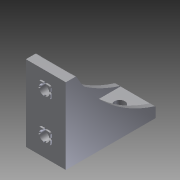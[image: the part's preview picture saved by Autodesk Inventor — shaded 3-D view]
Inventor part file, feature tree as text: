
AUTODESK INVENTOR PART (.ipt)
format: ipt  version: 2011 SP1 (Build 150282100, 282)  size: 227,840 bytes
history: native  units: mm
features: other x70, extrude x9, sketch x9, pattern_linear x2
ambient origin geometry x8: Origin, YZ Plane, XZ Plane, XY Plane, X Axis, Y Axis, Z Axis, Center Point
bodies: Solid1 (feature_tree)
feature tree (90):
  extrude  "Extrusion1"  Depth=15.0mm TaperAngle=0.0deg
  extrude  "Extrusion2"  Depth=5.0mm TaperAngle=0.0deg
  extrude  "Extrusion3"  Depth=5.0mm TaperAngle=0.0deg
  extrude  "Extrusion4"  Depth=0.8mm TaperAngle=0.0deg
  pattern_linear  "Rectangular Pattern1"  [2 undecoded]
  extrude  "Extrusion5"  [1 undecoded]
  pattern_linear  "Rectangular Pattern2"  [2 undecoded]
  extrude  "Extrusion6"  [1 undecoded]
  extrude  "Extrusion7"  [1 undecoded]
  extrude  "Extrusion8"  [1 undecoded]
  extrude  "Extrusion9"  [1 undecoded]
  other  "to_bolt_row_8_to_9_1_XY"
  other  "to_bolt_row_8_to_9_1_YZ"
  other  "to_bolt_row_8_to_9_1_ZX"
  other  "to_bolt_row_8_to_9_1_X"
  other  "to_bolt_row_8_to_9_1_Y"
  other  "to_bolt_row_8_to_9_1_Z"
  other  "to_bolt_row_8_to_9_1_Center"
  other  "to_bolt_row_8_to_9_2_XY"
  other  "to_bolt_row_8_to_9_2_YZ"
  other  "to_bolt_row_8_to_9_2_ZX"
  other  "to_bolt_row_8_to_9_2_X"
  other  "to_bolt_row_8_to_9_2_Y"
  other  "to_bolt_row_8_to_9_2_Z"
  other  "to_bolt_row_8_to_9_2_Center"
  other  "to_bolt_row_8_9_base_2_XY"
  other  "to_bolt_row_8_9_base_2_YZ"
  other  "to_bolt_row_8_9_base_2_ZX"
  other  "to_bolt_row_8_9_base_2_X"
  other  "to_bolt_row_8_9_base_2_Y"
  other  "to_bolt_row_8_9_base_2_Z"
  other  "to_bolt_row_8_9_base_2_Center"
  other  "to_bolt_row_8_9_base_1_XY"
  other  "to_bolt_row_8_9_base_1_YZ"
  other  "to_bolt_row_8_9_base_1_ZX"
  other  "to_bolt_row_8_9_base_1_X"
  other  "to_bolt_row_8_9_base_1_Y"
  other  "to_bolt_row_8_9_base_1_Z"
  other  "to_bolt_row_8_9_base_1_Center"
  other  "to_nut_row_8_to_9_2_XY"
  other  "to_nut_row_8_to_9_2_YZ"
  other  "to_nut_row_8_to_9_2_ZX"
  other  "to_nut_row_8_to_9_2_X"
  other  "to_nut_row_8_to_9_2_Y"
  other  "to_nut_row_8_to_9_2_Z"
  other  "to_nut_row_8_to_9_2_Center"
  other  "to_nut_row_8_to_9_1_XY"
  other  "to_nut_row_8_to_9_1_YZ"
  other  "to_nut_row_8_to_9_1_ZX"
  other  "to_nut_row_8_to_9_1_X"
  other  "to_nut_row_8_to_9_1_Y"
  other  "to_nut_row_8_to_9_1_Z"
  other  "to_nut_row_8_to_9_1_Center"
  other  "to_nut_row_8_9_base_2_XY"
  other  "to_nut_row_8_9_base_2_YZ"
  other  "to_nut_row_8_9_base_2_ZX"
  other  "to_nut_row_8_9_base_2_X"
  other  "to_nut_row_8_9_base_2_Y"
  other  "to_nut_row_8_9_base_2_Z"
  other  "to_nut_row_8_9_base_2_Center"
  other  "to_nut_row_8_9_base_1_XY"
  other  "to_nut_row_8_9_base_1_YZ"
  other  "to_nut_row_8_9_base_1_ZX"
  other  "to_nut_row_8_9_base_1_X"
  other  "to_nut_row_8_9_base_1_Y"
  other  "to_nut_row_8_9_base_1_Z"
  other  "to_nut_row_8_9_base_1_Center"
  other  "bracket_to_dummy_XY"
  other  "bracket_to_dummy_YZ"
  other  "bracket_to_dummy_ZX"
  other  "bracket_to_dummy_X"
  other  "bracket_to_dummy_Y"
  other  "bracket_to_dummy_Z"
  other  "bracket_to_dummy_Center"
  other  "bracket_to_bolt_XY"
  other  "bracket_to_bolt_YZ"
  other  "bracket_to_bolt_ZX"
  other  "bracket_to_bolt_X"
  other  "bracket_to_bolt_Y"
  other  "bracket_to_bolt_Z"
  other  "bracket_to_bolt_Center"
  sketch  "Sketch_15"  dims[d26=0.8mm d27=0.0mm]
  sketch  "Sketch_16"  dims[d28=1.25mm d29=0.0mm]
  sketch  "Sketch_28"
  sketch  "Sketch_6"  dims[d4=20.0mm d5=0.0mm d6=5.0mm d7=0.0mm]
  sketch  "Sketch_8"  dims[d8=20.0mm d10=20.0mm d11=10.0mm d13=0.0mm d14=5.0mm d15=0.0mm]
  sketch  "Sketch_1"  dims[d0=20.0mm d1=0.0mm d2=15.0mm d3=0.0mm]
  sketch  "Sketch_10"  dims[d16=20.0mm d18=15.0mm d19=10.0mm d21=0.0mm d22=0.8mm d23=0.0mm]
  sketch  "Sketch_13"  dims[d24=0.8mm d25=0.0mm]
  sketch  "Sketch_26"
note: 9 required parameter values undecoded (feature->parameter linkage not recoverable at this tier; creation-order binding heuristic only, values carry confidence <= 0.55)
